# Revit family: Rough-In_Box-Universal-Grohe-Rapido-35601
name_source: partatom
category: Plumbing Fixtures
units: mm (PartAtom-declared; Revit-internal decimal feet)

## family parameters
Cut with Voids When Loaded = Yes
Host = Face
OmniClass Number = 23.65.55.14.11
OmniClass Title = Inlet/Outlet Valves for Liquid Services
Part Type = Normal
Room Calculation Point = No
Round Connector Dimension = Use Diameter
Shared = Yes

## types (1)
- 35601000
    Assembly Code = D2020300
    CW Connection = Yes
    CWFU = 3
    Cold Water Connection Diameter = 1/2"
    Default Elevation = 40"
    Depth = 2 15/16"
    Description = Rapido Smartbox Universal Rough-In Box
    Finish = Plastic-GROHE-Blue
    HW Connection = Yes
    HWFU = 3
    Hot Water Connection Diameter = 1/2"
    Installation Type = In-Wall
    Length = 7 1/16"
    Manufacturer = Grohe
    Material = Plastic-GROHE-Blue
    Model = 35601000
    Port A = Yes
    Port A Connection = 1/2"
    Port A Connection Description = 1/2'' Global Outlet NPT-FIP
    Port B = Yes
    Port B Connection = 1/2"
    Port B Connection Description = 1/2''Global Outlet NPT-FIP
    Port C = Yes
    Port C Connection = 1/2"
    Port C Connection Description = 1/2'' Global Outlet NPT-FIP
    Price = Prices may vary. Please consult Manufacturer Representative for most up-to-date price list.
    Product Documentation Link = https://lixil.cdn.celum.cloud
    Product Page URL = https://www.grohe.ca
    Revised Date = 11/14/2023
    URL = https://www.grohe.ca
    Vent Connection = No
    WFU = 4
    Warranty Information = Limited Lifetime Warranty
    Waste Connection = No
    Width = 7 1/16"

## geometry (parser evidence)
native form markers: Sweep x2
no freeform markers — native parametric forms only
